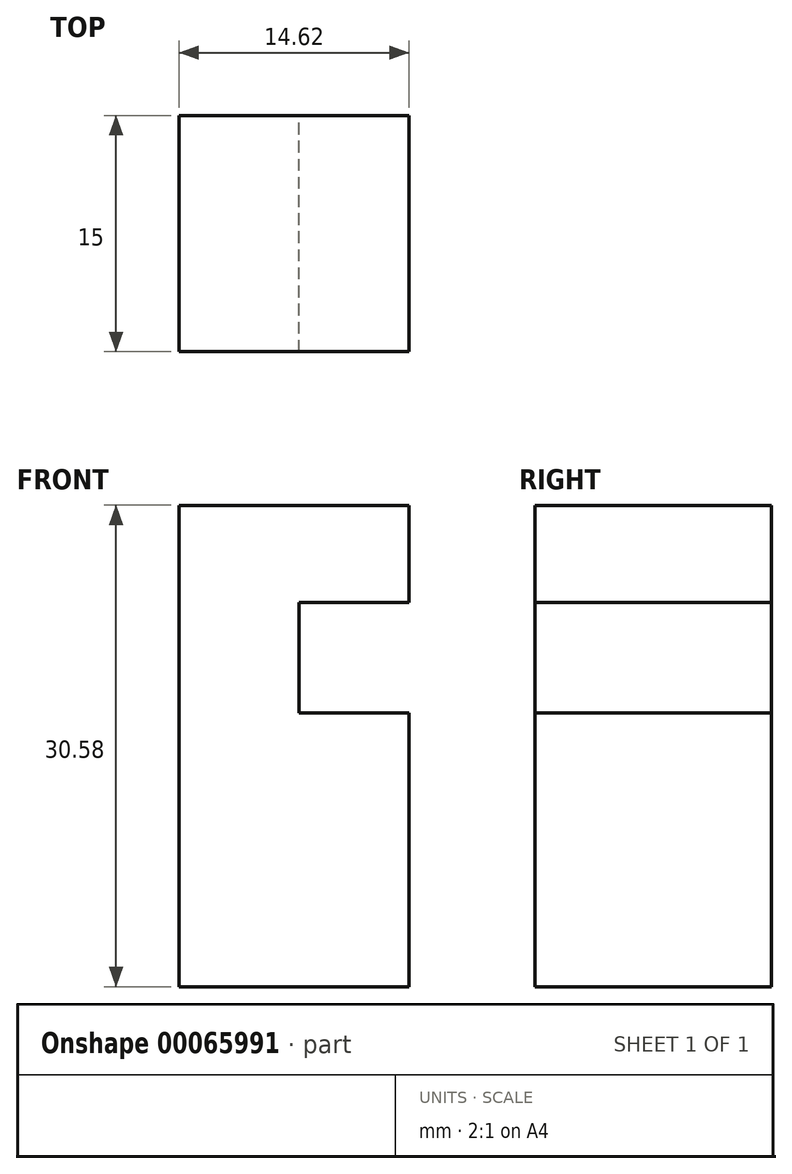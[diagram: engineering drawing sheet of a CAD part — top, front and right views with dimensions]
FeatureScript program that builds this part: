
annotation { "Feature Type Name" : "Feature", "Feature Type Description" : "" }
export const myFeature = defineFeature(function(context is Context, id is Id, definition is map)
    precondition{}
    {
        {
            var Q0;
            Q0=qCreatedBy(makeId("Front.planeOp"),FACE);
            var sketch = newSketch(context, id + "F0", { "sketchPlane" : qUnion([Q0])});
            skLineSegment(sketch, "E0", {"start": v(-0.87, 9) * mm, "end": v(-7.87, 9) * mm});
            skLineSegment(sketch, "E1", {"start": v(-7.87, 9) * mm, "end": v(-7.87, 2) * mm});
            skLineSegment(sketch, "E2", {"start": v(-7.87, 2) * mm, "end": v(-0.87, 2) * mm});
            skLineSegment(sketch, "E3", {"start": v(-0.87, 2) * mm, "end": v(-0.87, -15.4) * mm});
            skLineSegment(sketch, "E4", {"start": v(-0.87, -15.4) * mm, "end": v(-15.5, -15.4) * mm});
            skLineSegment(sketch, "E5", {"start": v(-15.5, 15.18) * mm, "end": v(-0.87, 15.18) * mm});
            skLineSegment(sketch, "E6", {"start": v(-0.87, 9) * mm, "end": v(-0.87, 15.18) * mm});
            skLineSegment(sketch, "E7.0", {"start": v(-15.5, -15.4) * mm, "end": v(-15.5, 15.18) * mm});
            skSolve(sketch);
        }
        {
            var Q0;
            Q0 = qSketchRegion(id + "F0", true);
            extrude(context, id + "F1", {"entities" : qUnion([Q0]), "depth" : 15 * mm});
        }
    });
